# Revit family: LVSD
name_source: partatom
category: Communication Devices
units: mm (PartAtom-declared; Revit-internal decimal feet)

## family parameters
Cut with Voids When Loaded = No
Host = Face
Maintain Annotation Orientation = No
OmniClass Number = 23.85.80.11.27
OmniClass Title = Lighting Controls
Part Type = Normal
Room Calculation Point = No
Round Connector Dimension = Use Diameter
Shared = Yes

## types (1)
- LVSD
    1 = Yes
    Assembly Code = D5090
    Black = Paint -  Carbon Black
    Default Elevation = 48 "
    Description = The Low Voltage dimmable switch station will provide manual control and 0-10V dimming for stand-alone applications. The Low Voltage dimmable switch station will also provide the customer with the opportunity to bring an already  Control Solutions project that utilizes stand-alone control packs and sensors to upgrade and install LED dimmable fixtures.Momentary, latching and a combination version containing a momentary and latching button provide flexibility to be used with our occupancy or vacancy control packs or a combination of both types.
    Features = Attractive, architecturally-pleasing decorator style design
• Gang-able with other decorator type devices
• Momentary version
• Latching version
• Combination Momentary and Latching version
• Works will all HCS Control and Auxiliary packs
• Pilot light function supported
• Provides 0-10V dimming control
• Low Voltage device: 24VDC
• Five-year limited warranty
    Height = 4.5 "
    Manufacturer = NX Lighting Controls
    Model = LVSD
    Operating Environment = Indoor use only
Operating temperature: 32°to 122°F (0° to 50°C)
Relative humidity (non-condensing): 10% to 90%
    Type Comments = Low Voltage Dimming Wall Switch
    URL = https://www.currentlighting.com
    Warranty = 5-Years Warranty
    White = Paint -  Matte White
    Width = 2.75 "

## geometry (parser evidence)
native form markers: Sweep x2
no freeform markers — native parametric forms only
